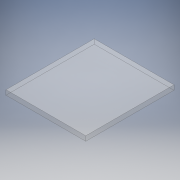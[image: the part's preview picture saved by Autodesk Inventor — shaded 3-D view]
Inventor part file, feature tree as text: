
AUTODESK INVENTOR PART (.ipt)
format: ipt  version: 2017 (Build 210142000, 142)  size: 111,104 bytes
history: native  units: mm
features: extrude x3, sketch x3
ambient origin geometry x8: Origin, YZ Plane, XZ Plane, XY Plane, X Axis, Y Axis, Z Axis, Center Point
bodies: Solid1 (feature_tree)
feature tree (6):
  extrude  "Extrusion1"  Depth=130.0mm
  extrude  "Extrusion2"  Depth=7.0mm
  extrude  "Extrusion3"  Depth=10.0mm TaperAngle=0.0deg
  sketch  "Sketch1"  dims[d0=335.0mm d1=130.0mm]
  sketch  "Sketch2"  dims[d2=7.0mm d3=0.0mm d7=100.0mm]
  sketch  "Sketch3"  dims[d8=10.0mm d9=0.0mm d10=10.0mm d11=0.0mm]
